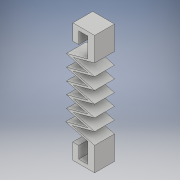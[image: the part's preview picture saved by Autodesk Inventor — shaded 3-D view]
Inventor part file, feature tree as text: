
AUTODESK INVENTOR PART (.ipt)
format: ipt  version: 2019 (Build 230136000, 136)  size: 151,552 bytes
history: native  units: in
note: dims shown in document units (in); Inventor stores cm internally (conversion verified against a paired STEP export)
features: extrude x1, sketch x1
ambient origin geometry x8: Origin, YZ Plane, XZ Plane, XY Plane, X Axis, Y Axis, Z Axis, Center Point
bodies: Body1 (feature_tree)
feature tree (2):
  extrude  "Extrusion2"  Depth=0.1575in
  sketch  "Sketch2"  dims[d9=0.3937in d14=0.1575in d15=0.0591in d16=0.2165in d17=0.2362in d18=0.1181in d19=0.0886in d24=0.1969in d25=0.1181in d28=0.0591in d29=0.0in d37=0.107in d38=0.5906in d39=0.1206in d40=0.0467in d41=0.1969in d42=0.0in]
